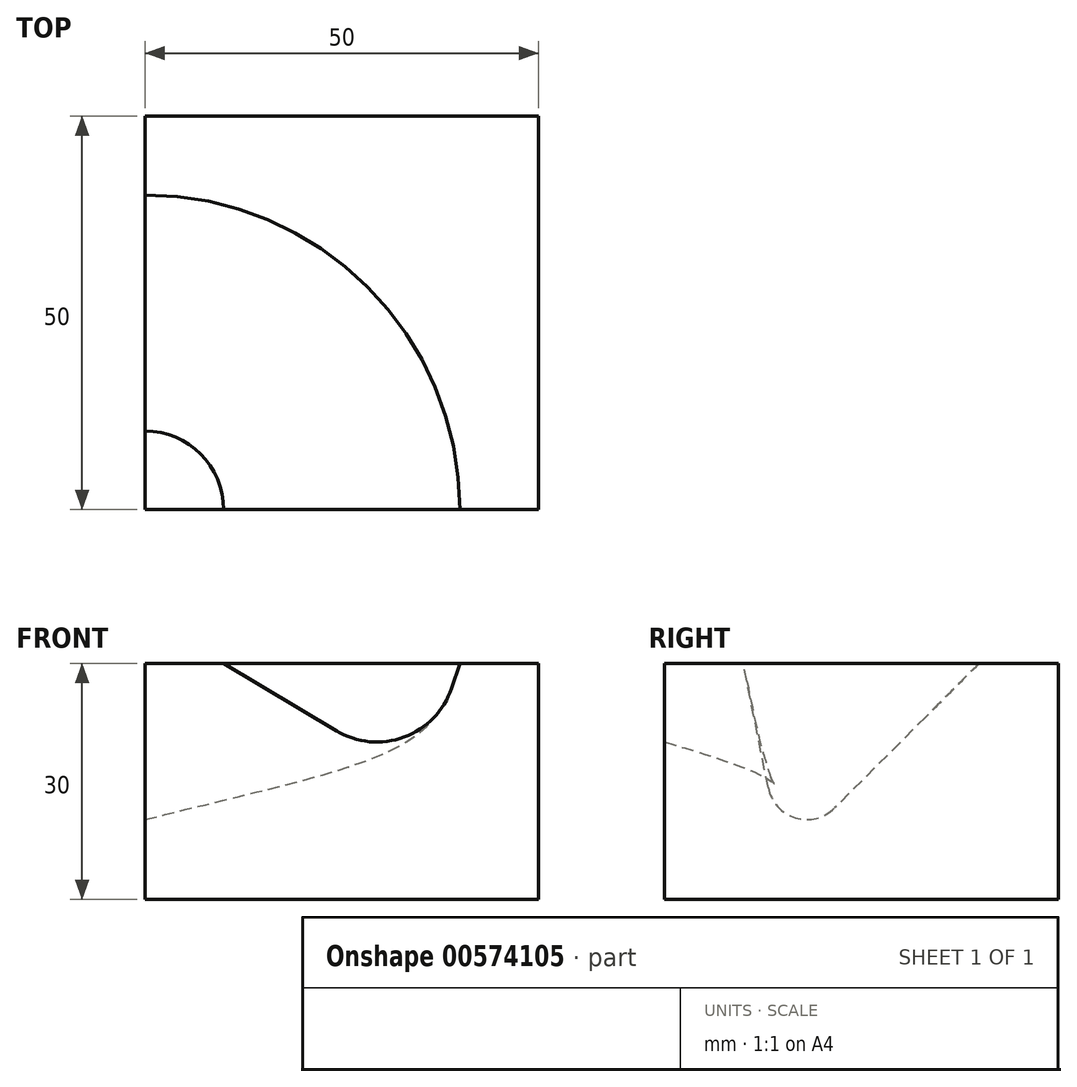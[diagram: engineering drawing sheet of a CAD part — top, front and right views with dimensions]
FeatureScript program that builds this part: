
annotation { "Feature Type Name" : "Feature", "Feature Type Description" : "" }
export const myFeature = defineFeature(function(context is Context, id is Id, definition is map)
    precondition{}
    {
        {
            var Q0;
            Q0=qCreatedBy(makeId("Top.planeOp"),FACE);
            var sketch = newSketch(context, id + "F0", { "sketchPlane" : qUnion([Q0])});
            skLineSegment(sketch, "E0.bottom", {"start": v(25, -25) * mm, "end": v(-25, -25) * mm});
            skLineSegment(sketch, "E0.top", {"start": v(25, 25) * mm, "end": v(-25, 25) * mm});
            skLineSegment(sketch, "E0.left", {"start": v(25, -25) * mm, "end": v(25, 25) * mm});
            skLineSegment(sketch, "E0.right", {"start": v(-25, -25) * mm, "end": v(-25, 25) * mm});
            skPoint(sketch, "E0.middle", {"position": v(0, 0) * mm});
            skArc(sketch, "E1", {"start": v(15, -25) * mm, "mid": v(3.28, 3.28) * mm, "end": v(-25, 15) * mm});
            skArc(sketch, "E2", {"start": v(-15, -25) * mm, "mid": v(-17.93, -17.93) * mm, "end": v(-25, -15) * mm});
            skSolve(sketch);
        }
        {
            var Q0;
            {var subQ1=sQuery(id+"F0.wireOp",EDGE,"E0.top");Q0=makeQuery(id+"F0.imprint","IMPRINT",FACE,{"disambiguationData":[TD([[makeQuery(id+"F0.imprint","IMPRINT",EDGE,{"derivedFrom":subQ1}),1.0]])]});}
            var Q1;
            {var subQ0=sQuery(id+"F0.wireOp",EDGE,"E1");Q1=makeQuery(id+"F0.imprint","IMPRINT",FACE,{"disambiguationData":[TD([[makeQuery(id+"F0.imprint","IMPRINT",EDGE,{"derivedFrom":subQ0}),1.0]])]});}
            var Q2;
            {var subQ3=sQuery(id+"F0.wireOp",EDGE,"E2");Q2=makeQuery(id+"F0.imprint","IMPRINT",FACE,{"disambiguationData":[TD([[makeQuery(id+"F0.imprint","IMPRINT",EDGE,{"derivedFrom":subQ3}),1.0]])]});}
            extrude(context, id + "F1", {"entities" : qUnion([Q0, Q1, Q2]), "oppositeDirection" : true, "depth" : 30 * mm, "offsetDistance" : 25 * mm});
        }
        {
            var Q0;
            Q0=makeQuery(id+"F1.opExtrude","SWEPT_FACE",FACE,{"disambiguationData":[OSD([sQuery(id+"F0.wireOp",EDGE,"E0.right")])]});
            var sketch = newSketch(context, id + "F2", { "sketchPlane" : qUnion([Q0])});
            skLineSegment(sketch, "E3", {"start": v(-15, 0) * mm, "end": v(3.4, -18.4) * mm});
            skLineSegment(sketch, "E4", {"start": v(11.83, -15.84) * mm, "end": v(15, 0) * mm});
            skArc(sketch, "E5", {"start": v(3.4, -18.4) * mm, "mid": v(8.38, -19.64) * mm, "end": v(11.83, -15.84) * mm});
            skPoint(sketch, "E6.orphan", {"position": v(10, -25) * mm});
            skSolve(sketch);
        }
        {
            var Q0;
            Q0=makeQuery(id+"F1.opExtrude","CAP_FACE",FACE,{"disambiguationData":[OSD([sQuery(id+"F0.wireOp",EDGE,"E0.bottom"),sQuery(id+"F0.wireOp",EDGE,"E0.top"),sQuery(id+"F0.wireOp",EDGE,"E0.left"),sQuery(id+"F0.wireOp",EDGE,"E0.right")])],"isStart":true});
            var sketch = newSketch(context, id + "F3", { "sketchPlane" : qUnion([Q0])});
            skArc(sketch, "E7", {"start": v(15, -25) * mm, "mid": v(3.28, 3.28) * mm, "end": v(-25, 15) * mm});
            skArc(sketch, "E8", {"start": v(-15, -25) * mm, "mid": v(-17.93, -17.93) * mm, "end": v(-25, -15) * mm});
            skSolve(sketch);
        }
        {
            var Q0;
            Q0=makeQuery(id+"F1.opExtrude","SWEPT_FACE",FACE,{"disambiguationData":[OSD([sQuery(id+"F0.wireOp",EDGE,"E0.bottom")])]});
            var sketch = newSketch(context, id + "F4", { "sketchPlane" : qUnion([Q0])});
            skLineSegment(sketch, "E9", {"start": v(-15, 0) * mm, "end": v(-0.69, -8.59) * mm});
            skLineSegment(sketch, "E10", {"start": v(13.94, -3.17) * mm, "end": v(15, 0) * mm});
            skArc(sketch, "E11", {"start": v(-0.69, -8.59) * mm, "mid": v(7.92, -9.4) * mm, "end": v(13.94, -3.17) * mm});
            skPoint(sketch, "E12.orphan", {"position": v(10, -15) * mm});
            skSolve(sketch);
        }
        {
            var Q1;
            {var subQ0=sQuery(id+"F2.wireOp",EDGE,"E3");Q1=makeQuery(id+"F2.imprint","IMPRINT",FACE,{"disambiguationData":[TD([[makeQuery(id+"F2.imprint","IMPRINT",EDGE,{"derivedFrom":subQ0}),1.0]])]});}
            var Q2;
            {var subQ0=sQuery(id+"F4.wireOp",EDGE,"E9");Q2=makeQuery(id+"F4.imprint","IMPRINT",FACE,{"disambiguationData":[TD([[makeQuery(id+"F4.imprint","IMPRINT",EDGE,{"derivedFrom":subQ0}),1.0]])]});}
            var Q3;
            Q3=sQuery(id+"F3.wireOp",EDGE,"E7");
            var Q4;
            Q4=sQuery(id+"F3.wireOp",EDGE,"E8");
            loft(context, id + "F5", {"operationType" : NewBodyOperationType.REMOVE, "addGuides" : true, "sheetProfilesArray" : [{ "sheetProfileEntities" : qUnion([Q1]) }, { "sheetProfileEntities" : qUnion([Q2]) }], "guidesArray" : [{ "guideEntities" : qUnion([Q3]), "guideDerivativeType" : LoftGuideDerivativeType.DEFAULT, "guideDerivativeMagnitude" : 1 }, { "guideEntities" : qUnion([Q4]), "guideDerivativeType" : LoftGuideDerivativeType.DEFAULT, "guideDerivativeMagnitude" : 1 }]});
        }
    });
